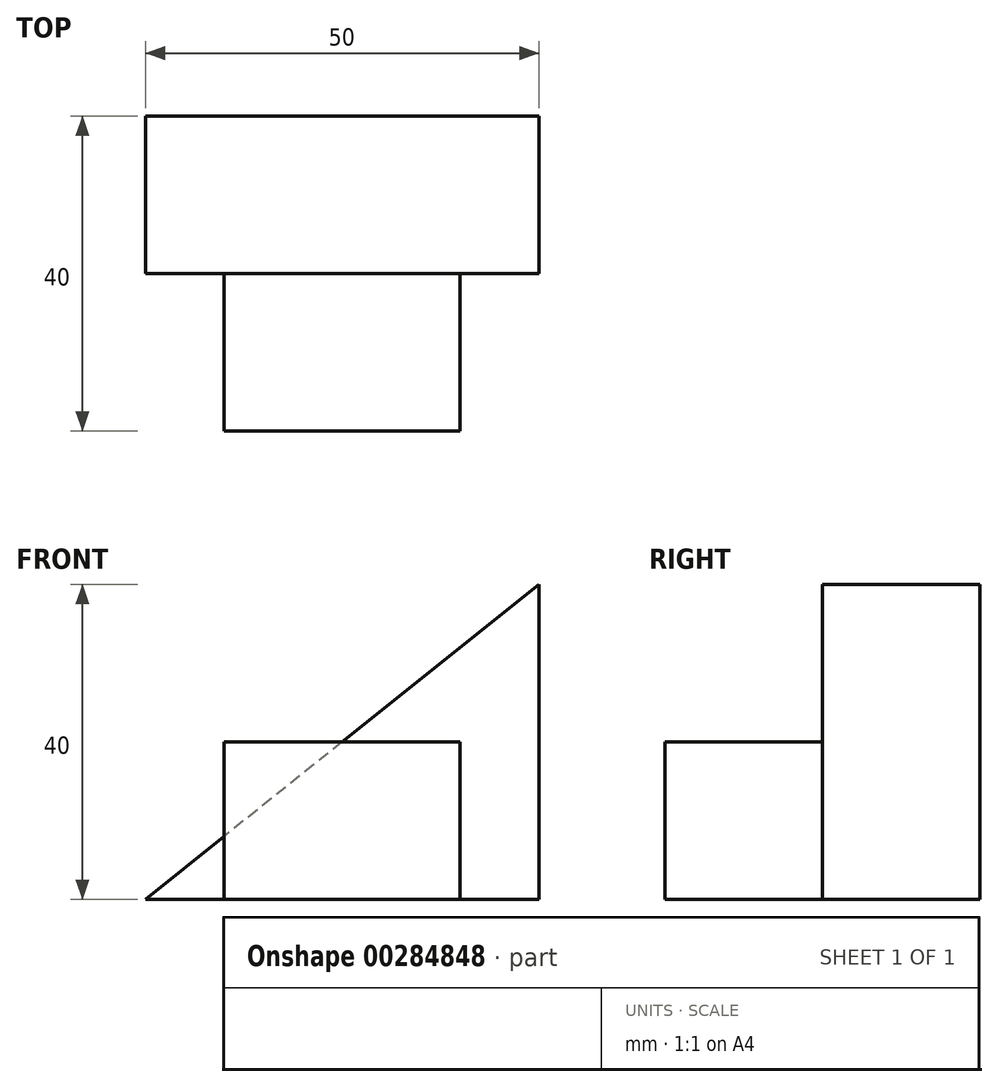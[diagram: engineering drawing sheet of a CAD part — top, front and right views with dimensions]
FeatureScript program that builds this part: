
annotation { "Feature Type Name" : "Feature", "Feature Type Description" : "" }
export const myFeature = defineFeature(function(context is Context, id is Id, definition is map)
    precondition{}
    {
        {
            var Q0;
            Q0=qCreatedBy(makeId("Front.planeOp"),FACE);
            var sketch = newSketch(context, id + "F0", { "sketchPlane" : qUnion([Q0])});
            skLineSegment(sketch, "E0.bottom", {"start": v(0, 0) * mm, "end": v(50, 0) * mm});
            skLineSegment(sketch, "E0.top", {"start": v(0, 40) * mm, "end": v(50, 40) * mm});
            skLineSegment(sketch, "E0.left", {"start": v(0, 0) * mm, "end": v(0, 40) * mm});
            skLineSegment(sketch, "E0.right", {"start": v(50, 0) * mm, "end": v(50, 40) * mm});
            skLineSegment(sketch, "E1", {"start": v(50, 40) * mm, "end": v(0, 0) * mm});
            skSolve(sketch);
        }
        {
            var Q0;
            Q0=makeQuery(id+"F0.imprint","IMPRINT",FACE,{"disambiguationData":[TD([[makeQuery(id+"F0.imprint","IMPRINT",EDGE,{"derivedFrom":sQuery(id+"F0.wireOp",EDGE,"E0.bottom")}),1.0]])]});
            extrude(context, id + "F1", {"entities" : qUnion([Q0]), "depth" : 20 * mm});
        }
        {
            var Q0;
            Q0=makeQuery(id+"F1.opExtrude","CAP_FACE",FACE,{"disambiguationData":[OSD([sQuery(id+"F0.wireOp",EDGE,"E0.bottom"),sQuery(id+"F0.wireOp",EDGE,"E0.top"),sQuery(id+"F0.wireOp",EDGE,"E0.left"),sQuery(id+"F0.wireOp",EDGE,"E0.right")])],"isStart":false});
            var sketch = newSketch(context, id + "F2", { "sketchPlane" : qUnion([Q0])});
            skLineSegment(sketch, "E2.bottom", {"start": v(10, 0) * mm, "end": v(40, 0) * mm});
            skLineSegment(sketch, "E2.top", {"start": v(10, 20) * mm, "end": v(40, 20) * mm});
            skLineSegment(sketch, "E2.left", {"start": v(10, 0) * mm, "end": v(10, 20) * mm});
            skLineSegment(sketch, "E2.right", {"start": v(40, 0) * mm, "end": v(40, 20) * mm});
            skSolve(sketch);
        }
        {
            var Q0;
            Q0=qSketchRegion(id+"F2",true);
            extrude(context, id + "F3", {"entities" : qUnion([Q0]), "operationType" : NewBodyOperationType.ADD, "depth" : 20 * mm});
        }
    });
